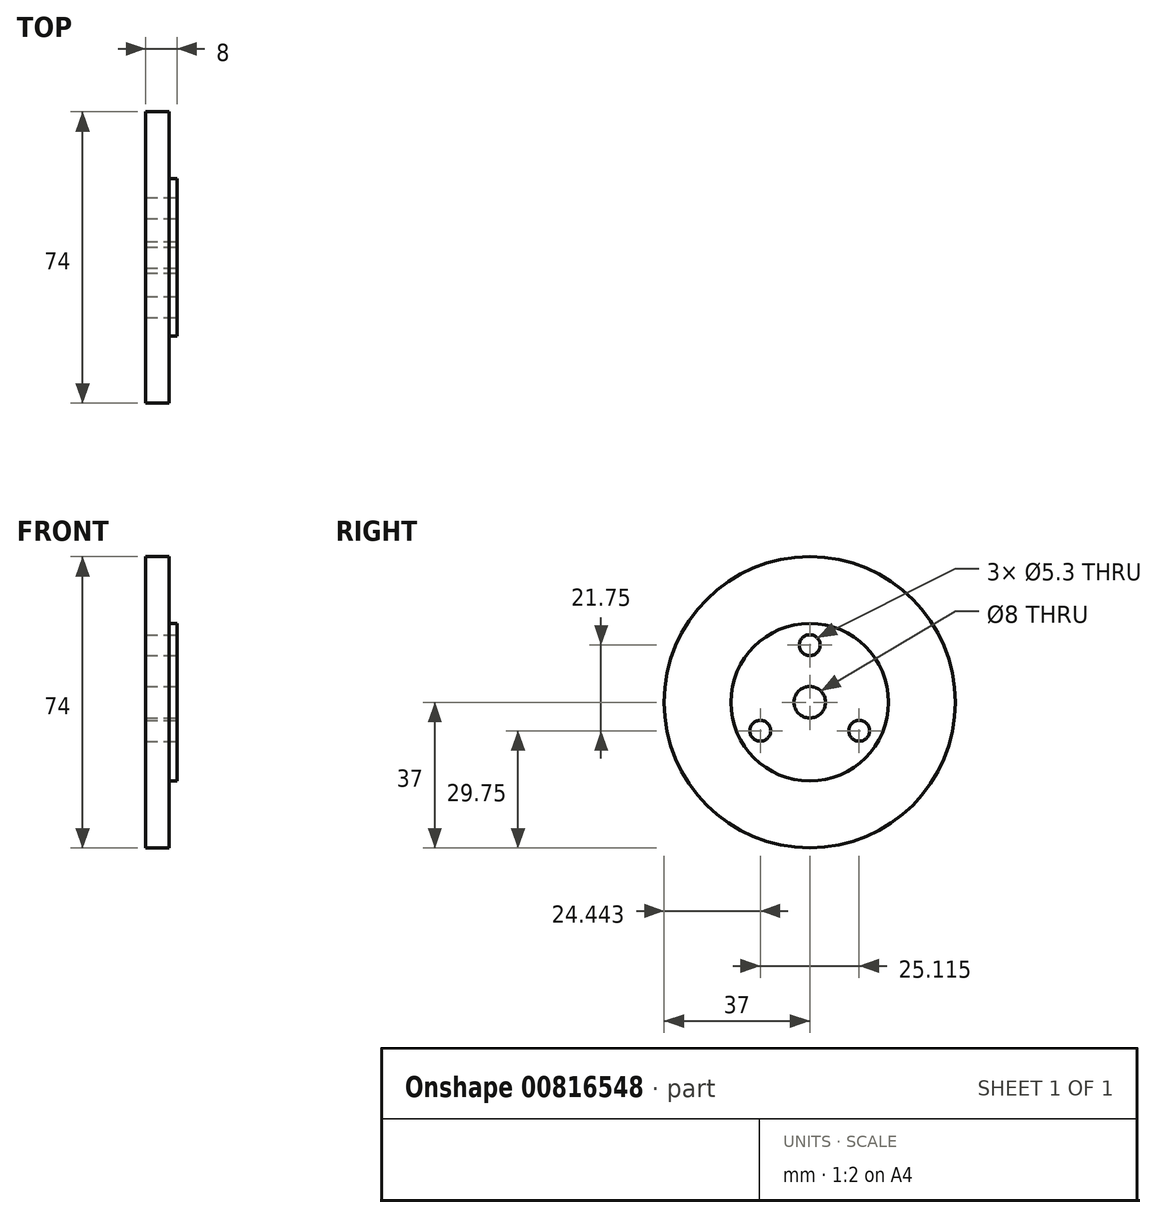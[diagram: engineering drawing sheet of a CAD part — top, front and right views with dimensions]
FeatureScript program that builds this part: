
annotation { "Feature Type Name" : "Feature", "Feature Type Description" : "" }
export const myFeature = defineFeature(function(context is Context, id is Id, definition is map)
    precondition{}
    {
        {
            var Q0;
            Q0=qCreatedBy(makeId("Right.planeOp"),FACE);
            var sketch = newSketch(context, id + "F0", { "sketchPlane" : qUnion([Q0])});
            skCircle(sketch, "E0", {"center": v(0, 0) * mm, "radius": 37 * mm});
            skCircle(sketch, "E1", {"center": v(0, 0) * mm, "radius": 4 * mm});
            skLineSegment(sketch, "E2", {"start": v(0, 50.53) * mm, "end": v(0, -45.3) * mm, "construction": true});
            skLineSegment(sketch, "E3", {"start": v(0, 0) * mm, "end": v(28.08, 48.64) * mm, "construction": true});
            skLineSegment(sketch, "E4", {"start": v(0, 0) * mm, "end": v(48.73, -28.13) * mm, "construction": true});
            skLineSegment(sketch, "E5.MirrorCS", {"start": v(43.76, 25.27) * mm, "end": v(-39.22, -22.65) * mm, "construction": true});
            skLineSegment(sketch, "E6.MirrorCS", {"start": v(0, 0) * mm, "end": v(-28.08, 48.64) * mm, "construction": true});
            skLineSegment(sketch, "E7.MirrorCS", {"start": v(-43.76, 25.27) * mm, "end": v(39.22, -22.65) * mm, "construction": true});
            skLineSegment(sketch, "E8.MirrorCS", {"start": v(0, 0) * mm, "end": v(-28.08, -48.64) * mm, "construction": true});
            skLineSegment(sketch, "E9.MirrorCS", {"start": v(0, 0) * mm, "end": v(28.08, -48.64) * mm, "construction": true});
            skPoint(sketch, "E10.visualSharp", {"position": v(0, 32) * mm});
            skPoint(sketch, "E11.visualSharp", {"position": v(-14.73, 8.5) * mm});
            skArc(sketch, "E11.filletArc", {"start": v(-14.54, 8.81) * mm, "mid": v(-14.73, 8.5) * mm, "end": v(-14.9, 8.18) * mm});
            skPoint(sketch, "E12.visualSharp", {"position": v(-27.71, -16) * mm});
            skPoint(sketch, "E13.visualSharp", {"position": v(27.71, -16) * mm});
            skCircle(sketch, "E14", {"center": v(0, 0) * mm, "radius": 14.5 * mm, "construction": true});
            skCircle(sketch, "E15", {"center": v(-12.56, -7.25) * mm, "radius": 2.65 * mm});
            skCircle(sketch, "E16", {"center": v(12.56, -7.25) * mm, "radius": 2.65 * mm});
            skCircle(sketch, "E17", {"center": v(0, 14.5) * mm, "radius": 2.65 * mm});
            skCircle(sketch, "E18", {"center": v(0, 0) * mm, "radius": 20 * mm});
            skSolve(sketch);
        }
        {
            var Q0;
            Q0=qSketchRegion(id+"F0",true);
            var Q1;
            Q1=makeQuery(id+"F0.imprint","IMPRINT",FACE,{"disambiguationData":[TD([[makeQuery(id+"F0.imprint","IMPRINT",EDGE,{"derivedFrom":sQuery(id+"F0.wireOp",EDGE,"E1")}),-1.0]])]});
            var Q2;
            Q2=makeQuery(id+"F0.imprint","IMPRINT",FACE,{"disambiguationData":[TD([[makeQuery(id+"F0.imprint","IMPRINT",EDGE,{"derivedFrom":sQuery(id+"F0.wireOp",EDGE,"fmaITuh8-1pOd-9VWb-JPiM-VdxlWLn1jFGd")}),-1.0]])]});
            extrude(context, id + "F1", {"entities" : qUnion([Q0, Q1, Q2]), "oppositeDirection" : true, "depth" : 8 * mm, "offsetDistance" : 25 * mm});
        }
        {
            var Q0;
            Q0=makeQuery(id+"F0.imprint","IMPRINT",FACE,{"disambiguationData":[TD([[makeQuery(id+"F0.imprint","IMPRINT",EDGE,{"derivedFrom":sQuery(id+"F0.wireOp",EDGE,"E0")}),1.0]])]});
            extrude(context, id + "F2", {"entities" : qUnion([Q0]), "operationType" : NewBodyOperationType.REMOVE, "oppositeDirection" : true, "depth" : 2 * mm, "offsetDistance" : 25 * mm});
        }
    });
